# Revit family: rba-bim-B39619
name_source: partatom
category: Specialty Equipment
revit_build: Autodesk Revit 2018 (Build: 20170223_1515(x64)
units: mm (PartAtom-declared; Revit-internal decimal feet)

## family parameters
Always vertical = No
Cut with Voids When Loaded = No
Part Type = Normal
Room Calculation Point = No
Round Connector Dimension = Use Diameter
Shared = Yes
Work Plane-Based = Yes

## types (1)
- B-39619
    Default Elevation = 0 mm  [stored 0 ft]
    Description = Bobrick Paper Towel Roll & Waste ClassicSeries ®| Surface Mounted
    Keynote = Unit includes convertible universal, roll paper towel module and 12‑gallon (45.5-L) waste receptacle module which can be interchanged with an automatic, universal or folded towel module and 18-gallon waste receptacle module, respectively. Cabinet is not replaced when changing modules. Satin-finish stainless steel. Seamless beveled flange. Touch-free, pull-towel mechanism dispenses 12" (305mm) length per pull of universal roll paper towels. Accommodates 8" (205mm) wide, up to 8" (205mm) diameter rolls, 800 ft (244m) long, plus 3 1⁄2" (90mm) diameter stub roll with automatic transfer. Removable waste receptacle is locked into cabinet. Skirt for surface-mounting.
ADD TO PROJECT SUBMITTAL BUILDER
ADD TO PROJECT SPEC
    Manufacturer = Bobrick Washroom Equipment
    Materials and Finishes = Stainless Steel Satin Finish
    Model = B-39619
    Modified Issue = 20200825.01
    Product URL = http://www.bobrick.com
    Revised Date = 27/08/2013
    URL = www.rba.com.au

note: [stored X ft] marks values corroborated as IEEE doubles in the binary element streams (Revit-internal decimal feet)

## geometry (parser evidence)
native form markers: Blend x4, Sweep x3
no freeform markers — native parametric forms only
